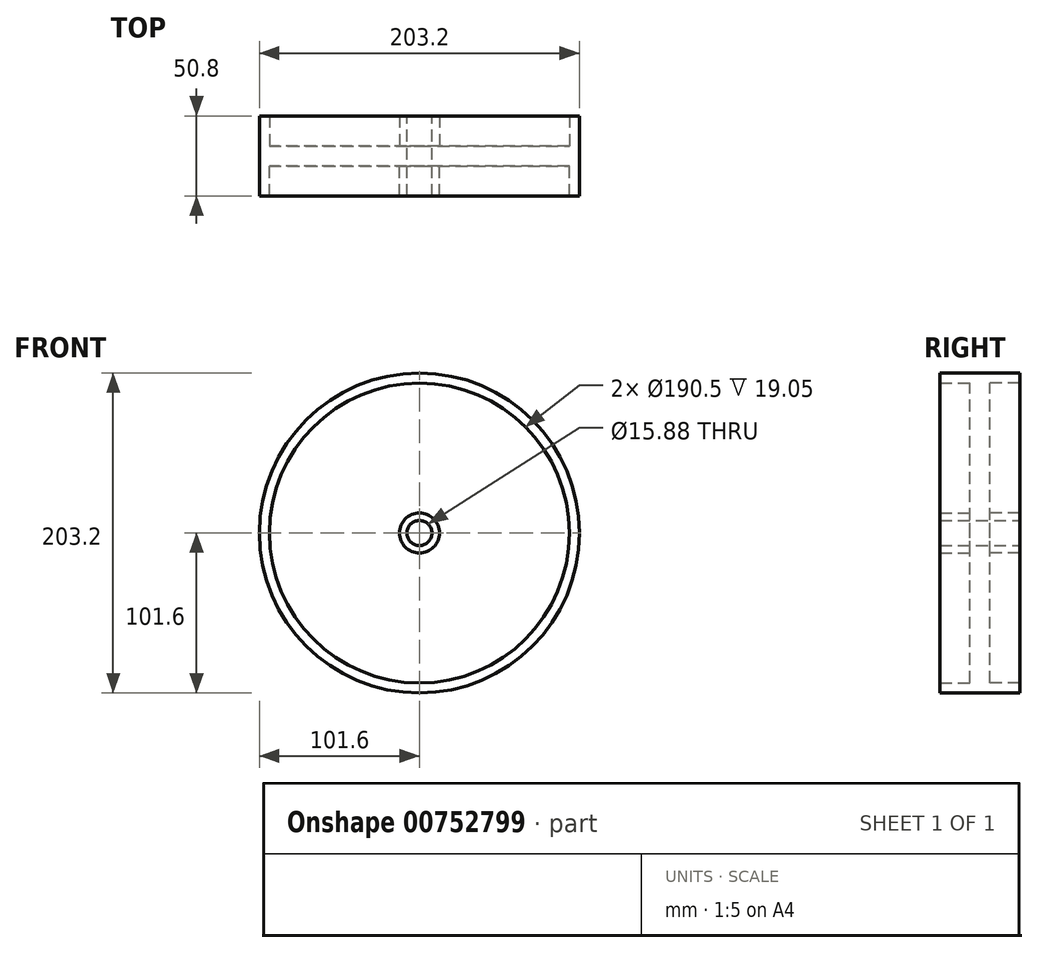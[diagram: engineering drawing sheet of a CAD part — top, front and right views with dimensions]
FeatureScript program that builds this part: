
annotation { "Feature Type Name" : "Feature", "Feature Type Description" : "" }
export const myFeature = defineFeature(function(context is Context, id is Id, definition is map)
    precondition{}
    {
        {
            var Q0;
            Q0=qCreatedBy(makeId("Front.planeOp"),FACE);
            var sketch = newSketch(context, id + "F0", { "sketchPlane" : qUnion([Q0])});
            skCircle(sketch, "E0", {"center": v(0, 0) * mm, "radius": 101.6 * mm});
            skCircle(sketch, "E1", {"center": v(0, 0) * mm, "radius": 7.94 * mm});
            skSolve(sketch);
        }
        {
            var Q0;
            Q0=makeQuery(id+"F0.imprint","IMPRINT",FACE,{"disambiguationData":[TD([[makeQuery(id+"F0.imprint","IMPRINT",EDGE,{"derivedFrom":sQuery(id+"F0.wireOp",EDGE,"E0")}),1.0]])]});
            extrude(context, id + "F1", {"entities" : qUnion([Q0]), "depth" : 6.35 * mm, "offsetDistance" : 25.4 * mm});
        }
        {
            var Q0;
            Q0=makeQuery(id+"F1.opExtrude","CAP_FACE",FACE,{"disambiguationData":[OSD([sQuery(id+"F0.wireOp",EDGE,"E0"),sQuery(id+"F0.wireOp",EDGE,"E1")])],"isStart":false});
            var sketch = newSketch(context, id + "F2", { "sketchPlane" : qUnion([Q0])});
            skCircle(sketch, "E2", {"center": v(0, 0) * mm, "radius": 101.6 * mm});
            skCircle(sketch, "E3", {"center": v(0, 0) * mm, "radius": 95.25 * mm});
            skCircle(sketch, "E4", {"center": v(0, 0) * mm, "radius": 12.7 * mm});
            skCircle(sketch, "E5", {"center": v(0, 0) * mm, "radius": 7.94 * mm});
            skSolve(sketch);
        }
        {
            var Q0;
            Q0=makeQuery(id+"F2.imprint","IMPRINT",FACE,{"disambiguationData":[TD([[makeQuery(id+"F2.imprint","IMPRINT",EDGE,{"derivedFrom":sQuery(id+"F2.wireOp",EDGE,"E2")}),1.0]])]});
            var Q1;
            Q1=makeQuery(id+"F2.imprint","IMPRINT",FACE,{"disambiguationData":[TD([[makeQuery(id+"F2.imprint","IMPRINT",EDGE,{"derivedFrom":sQuery(id+"F2.wireOp",EDGE,"E4")}),1.0]])]});
            extrude(context, id + "F3", {"entities" : qUnion([Q0, Q1]), "operationType" : NewBodyOperationType.ADD, "depth" : 19.05 * mm, "offsetDistance" : 25.4 * mm});
        }
        {
            var Q0;
            Q0=makeQuery(id+"F1.opExtrude","SWEPT_BODY",BODY,{"disambiguationData":[OSD([sQuery(id+"F0.wireOp",EDGE,"E0"),sQuery(id+"F0.wireOp",EDGE,"E1")])]});
            var Q1;
            Q1=qCreatedBy(makeId("Front.planeOp"),FACE);
            mirror(context, id + "F4", {"operationType" : NewBodyOperationType.ADD, "entities" : qUnion([Q0]), "mirrorPlane" : qUnion([Q1])});
        }
    });
